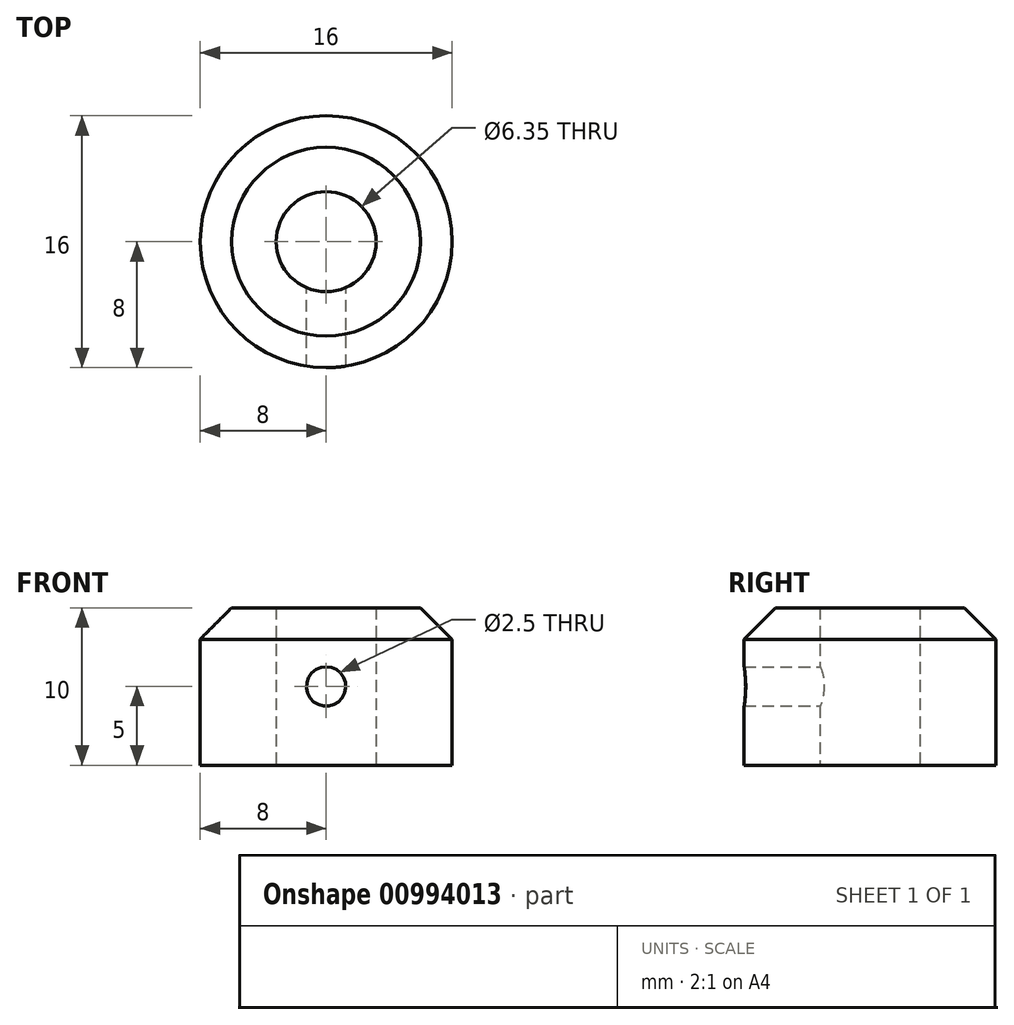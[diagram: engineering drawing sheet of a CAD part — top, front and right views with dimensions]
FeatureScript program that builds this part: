
annotation { "Feature Type Name" : "Feature", "Feature Type Description" : "" }
export const myFeature = defineFeature(function(context is Context, id is Id, definition is map)
    precondition{}
    {
        {
            var Q0;
            Q0=qCreatedBy(makeId("Front.planeOp"),FACE);
            var sketch = newSketch(context, id + "F0", { "sketchPlane" : qUnion([Q0])});
            skCircle(sketch, "E0", {"center": v(0, 3.17) * mm, "radius": 3.17 * mm, "construction": true});
            skLineSegment(sketch, "E1", {"start": v(3.18, 0) * mm, "end": v(8, 0) * mm});
            skLineSegment(sketch, "E2", {"start": v(8, 0) * mm, "end": v(8, 3.59) * mm});
            skLineSegment(sketch, "E3", {"start": v(5.17, 10) * mm, "end": v(3.17, 10) * mm});
            skLineSegment(sketch, "E4", {"start": v(3.17, 10) * mm, "end": v(3.18, 0) * mm});
            skPoint(sketch, "E5.visualSharp", {"position": v(8, 0) * mm});
            skPoint(sketch, "E6.visualSharp", {"position": v(5.17, 6.83) * mm});
            skPoint(sketch, "E7.visualSharp", {"position": v(5.17, 10) * mm});
            skLineSegment(sketch, "E8", {"start": v(0, 0) * mm, "end": v(0, 14.33) * mm, "construction": true});
            skLineSegment(sketch, "E9", {"start": v(8, 3.59) * mm, "end": v(8, 8) * mm});
            skLineSegment(sketch, "E10", {"start": v(8, 8) * mm, "end": v(6, 10) * mm});
            skLineSegment(sketch, "E11", {"start": v(6, 10) * mm, "end": v(5.17, 10) * mm});
            skSolve(sketch);
        }
        {
            var Q0;
            Q0=makeQuery(id+"F0.imprint","IMPRINT",FACE,{"disambiguationData":[TD([[makeQuery(id+"F0.imprint","IMPRINT",EDGE,{"derivedFrom":sQuery(id+"F0.wireOp",EDGE,"E1")}),1.0]])]});
            var Q1;
            Q1=sQuery(id+"F0.wireOp",EDGE,"E8");
            revolve(context, id + "F1", {"surfaceOperationType" : NewSurfaceOperationType.NEW, "entities" : qUnion([Q0]), "axis" : qUnion([Q1]), "revolveType" : RevolveType.FULL});
        }
        {
            var Q0;
            Q0=qCreatedBy(makeId("Front.planeOp"),FACE);
            var sketch = newSketch(context, id + "F2", { "sketchPlane" : qUnion([Q0])});
            skCircle(sketch, "E12", {"center": v(0, 5) * mm, "radius": 1.25 * mm});
            skSolve(sketch);
        }
        {
            var Q0;
            Q0 = qSketchRegion(id + "F2", true);
            extrude(context, id + "F3", {"entities" : qUnion([Q0]), "operationType" : NewBodyOperationType.REMOVE, "depth" : 25 * mm, "offsetDistance" : 25 * mm});
        }
    });
